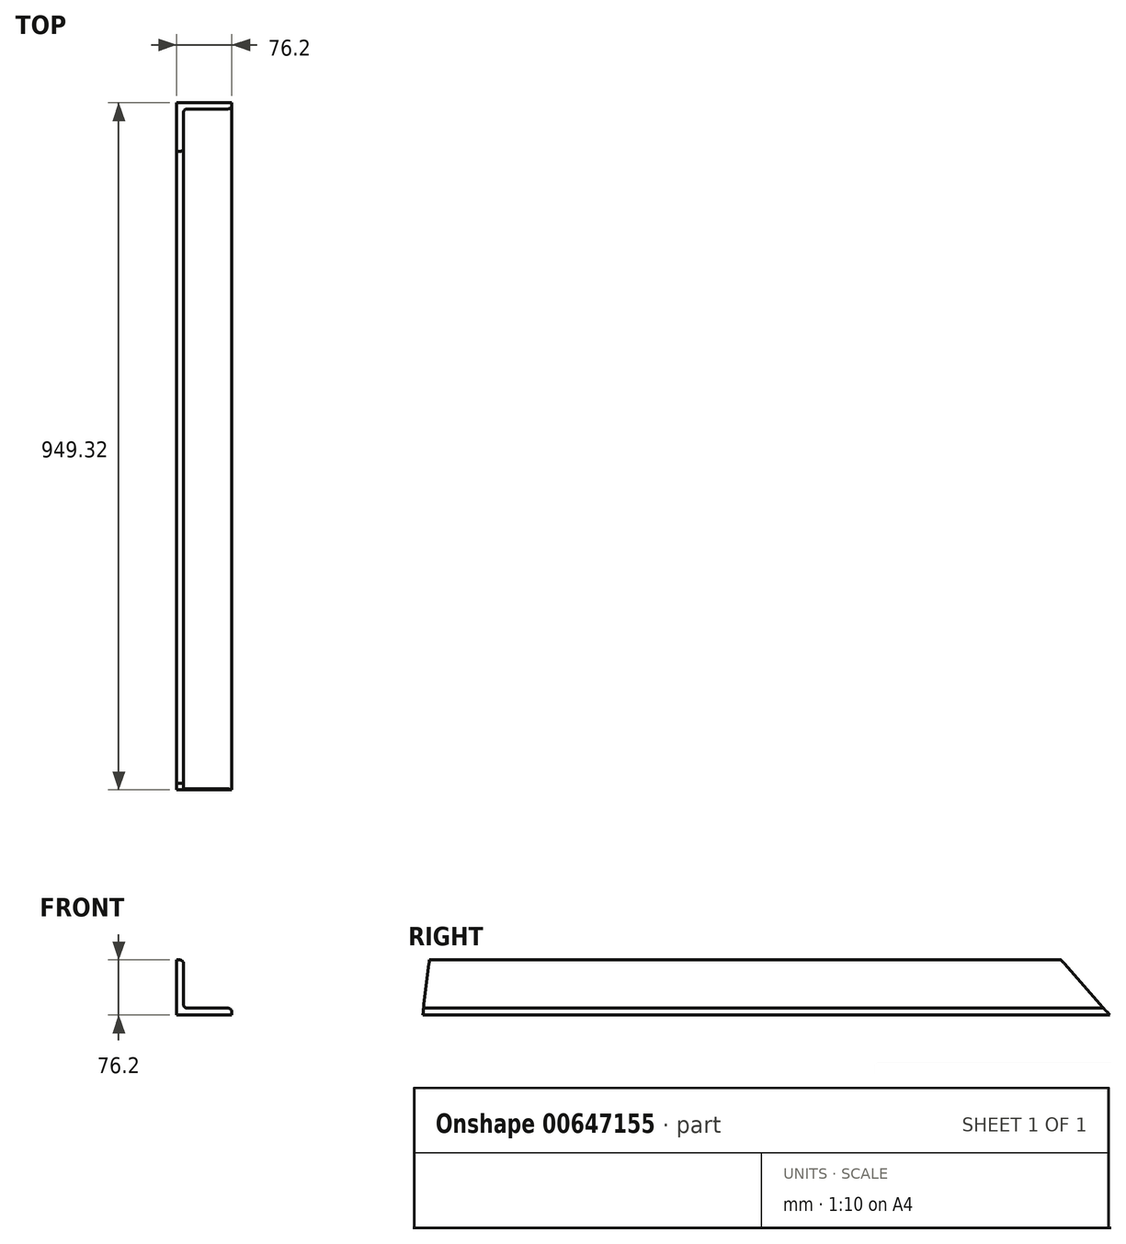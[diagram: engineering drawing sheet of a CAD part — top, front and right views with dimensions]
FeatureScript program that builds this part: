
annotation { "Feature Type Name" : "Feature", "Feature Type Description" : "" }
export const myFeature = defineFeature(function(context is Context, id is Id, definition is map)
    precondition{}
    {
        {
            var Q0;
            Q0=qCreatedBy(makeId("Front.planeOp"),FACE);
            var sketch = newSketch(context, id + "F0", { "sketchPlane" : qUnion([Q0])});
            skLineSegment(sketch, "E0.bottom", {"start": v(0, 0) * mm, "end": v(76.2, 0) * mm});
            skLineSegment(sketch, "E0.top", {"start": v(0, 76.2) * mm, "end": v(9.52, 76.2) * mm});
            skLineSegment(sketch, "E0.left", {"start": v(0, 0) * mm, "end": v(0, 76.2) * mm});
            skLineSegment(sketch, "E0.right", {"start": v(76.2, 0) * mm, "end": v(76.2, 9.53) * mm});
            skLineSegment(sketch, "E1.0", {"start": v(9.52, 9.53) * mm, "end": v(9.52, 76.2) * mm});
            skLineSegment(sketch, "E2.0", {"start": v(9.52, 9.53) * mm, "end": v(76.2, 9.53) * mm});
            skSolve(sketch);
        }
        {
            var Q0;
            Q0 = qSketchRegion(id + "F0", true);
            extrude(context, id + "F1", {"entities" : qUnion([Q0]), "endBound" : BoundingType.SYMMETRIC, "depth" : 949.32 * mm, "offsetDistance" : 25.4 * mm});
        }
        {
            var Q0;
            Q0=makeQuery(id+"F1.opExtrude","SWEPT_EDGE",EDGE,{"disambiguationData":[OSD([sQuery(id+"F0.wireOp",EDGE,"E0.top"),sQuery(id+"F0.wireOp",EDGE,"E1.0")])]});
            var Q1;
            Q1=makeQuery(id+"F1.opExtrude","SWEPT_EDGE",EDGE,{"disambiguationData":[OSD([sQuery(id+"F0.wireOp",EDGE,"E1.0"),sQuery(id+"F0.wireOp",EDGE,"E2.0")])]});
            var Q2;
            Q2=makeQuery(id+"F1.opExtrude","SWEPT_EDGE",EDGE,{"disambiguationData":[OSD([sQuery(id+"F0.wireOp",EDGE,"E0.right"),sQuery(id+"F0.wireOp",EDGE,"E2.0")])]});
            fillet(context, id + "F2", {"entities" : qUnion([Q0, Q1, Q2]), "radius" : 5.08 * mm, "tangentPropagation" : true, "allowEdgeOverflow" : false});
        }
        {
            var Q0;
            Q0=makeQuery(id+"F1.opExtrude","SWEPT_FACE",FACE,{"disambiguationData":[OSD([sQuery(id+"F0.wireOp",EDGE,"E0.left")])]});
            var sketch = newSketch(context, id + "F3", { "sketchPlane" : qUnion([Q0])});
            skPoint(sketch, "E3.0", {"position": v(-474.66, 0) * mm});
            skLineSegment(sketch, "E4", {"start": v(-474.66, 0) * mm, "end": v(-407.48, 76.2) * mm});
            skLineSegment(sketch, "E5", {"start": v(-407.48, 76.2) * mm, "end": v(-474.66, 76.2) * mm});
            skLineSegment(sketch, "E6", {"start": v(-474.66, 76.2) * mm, "end": v(-474.66, 0) * mm});
            skPoint(sketch, "E7.0", {"position": v(474.66, 0) * mm});
            skLineSegment(sketch, "E8", {"start": v(474.66, 0) * mm, "end": v(465.3, 76.2) * mm});
            skLineSegment(sketch, "E9", {"start": v(465.3, 76.2) * mm, "end": v(474.66, 76.2) * mm});
            skLineSegment(sketch, "E10", {"start": v(474.66, 76.2) * mm, "end": v(474.66, 0) * mm});
            skSolve(sketch);
        }
        {
            var Q0;
            Q0 = qSketchRegion(id + "F3", true);
            extrude(context, id + "F4", {"entities" : qUnion([Q0]), "operationType" : NewBodyOperationType.REMOVE, "oppositeDirection" : true, "depth" : 76.2 * mm, "offsetDistance" : 25.4 * mm});
        }
        {
            var Q0;
            Q0 = qSketchRegion(id + "F3", true);
            extrude(context, id + "F5", {"entities" : qUnion([Q0]), "operationType" : NewBodyOperationType.REMOVE, "oppositeDirection" : true, "depth" : 76.2 * mm, "offsetDistance" : 25.4 * mm});
        }
    });
